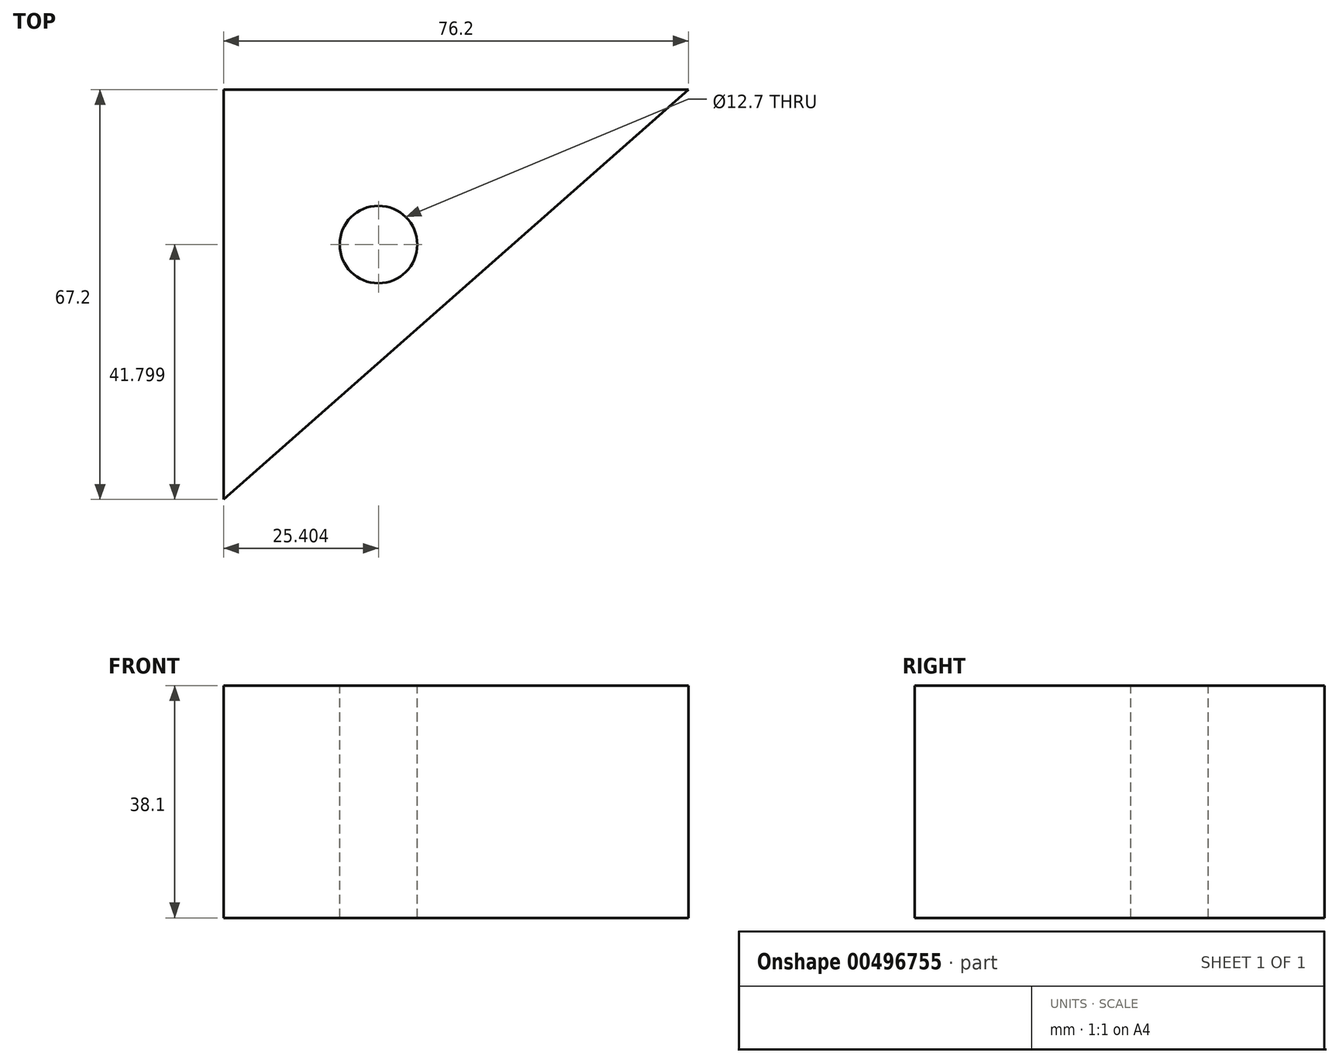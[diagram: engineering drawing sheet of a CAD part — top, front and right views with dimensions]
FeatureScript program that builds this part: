
annotation { "Feature Type Name" : "Feature", "Feature Type Description" : "" }
export const myFeature = defineFeature(function(context is Context, id is Id, definition is map)
    precondition{}
    {
        {
            var Q0;
            Q0=qCreatedBy(makeId("Top.planeOp"),FACE);
            var sketch = newSketch(context, id + "F0", { "sketchPlane" : qUnion([Q0])});
            skLineSegment(sketch, "E0", {"start": v(-35.97, -34.8) * mm, "end": v(-35.97, 32.4) * mm});
            skLineSegment(sketch, "E1", {"start": v(-35.97, 32.4) * mm, "end": v(40.23, 32.4) * mm});
            skLineSegment(sketch, "E2", {"start": v(40.23, 32.4) * mm, "end": v(-35.97, -34.8) * mm});
            skSolve(sketch);
        }
        {
            var Q0;
            Q0=makeQuery(id+"F0.imprint","IMPRINT",FACE,{"disambiguationData":[TD([[makeQuery(id+"F0.imprint","IMPRINT",EDGE,{"derivedFrom":sQuery(id+"F0.wireOp",EDGE,"E0")}),-1.0]])]});
            extrude(context, id + "F1", {"entities" : qUnion([Q0]), "depth" : 38.1 * mm});
        }
        {
            var Q0;
            Q0=makeQuery(id+"F1.opExtrude","CAP_FACE",FACE,{"disambiguationData":[OSD([sQuery(id+"F0.wireOp",EDGE,"E0"),sQuery(id+"F0.wireOp",EDGE,"E1"),sQuery(id+"F0.wireOp",EDGE,"E2")])],"isStart":false});
            var sketch = newSketch(context, id + "F2", { "sketchPlane" : qUnion([Q0])});
            skPoint(sketch, "E3", {"position": v(-10.57, 7) * mm});
            skSolve(sketch);
        }
        {
            var Q0;
            Q0=sQuery(id+"F2.wireOp",VERTEX,"E3");
            var Q1;
            Q1=makeQuery(id+"F1.opExtrude","SWEPT_BODY",BODY,{"disambiguationData":[OSD([sQuery(id+"F0.wireOp",EDGE,"E0"),sQuery(id+"F0.wireOp",EDGE,"E1"),sQuery(id+"F0.wireOp",EDGE,"E2")])]});
            hole(context, id + "F3", {"style" : HoleStyle.C_BORE, "endStyle" : HoleEndStyle.THROUGH, "holeDiameter" : 6.35 * mm, "cBoreDiameter" : 12.7 * mm, "cBoreDepth" : 76.2 * mm, "isTappedThrough" : true, "tappedDepth" : 12.7 * mm, "tapClearance" : 3, "locations" : qUnion([Q0]), "scope" : qUnion([Q1])});
        }
    });
